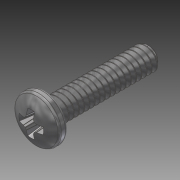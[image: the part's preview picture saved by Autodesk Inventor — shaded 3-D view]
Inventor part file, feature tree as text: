
AUTODESK INVENTOR PART (.ipt)
format: ipt  version: 2014 SP1 (Build 180222100, 222)  size: 772,096 bytes
history: native  units: in
note: dims shown in document units (in); Inventor stores cm internally (conversion verified against a paired STEP export)
features: fillet x1, other x1, imported_body x1
ambient origin geometry x8: Origin, YZ Plane, XZ Plane, XY Plane, X Axis, Y Axis, Z Axis, Center Point
bodies: Body1 (feature_tree)
feature tree (3):
  fillet  "Fillet1"  [1 undecoded]
  other  "91772A1101"
  imported_body  "Base1"
note: 1 required parameter value undecoded (feature->parameter linkage not recoverable at this tier; creation-order binding heuristic only, values carry confidence <= 0.55)
